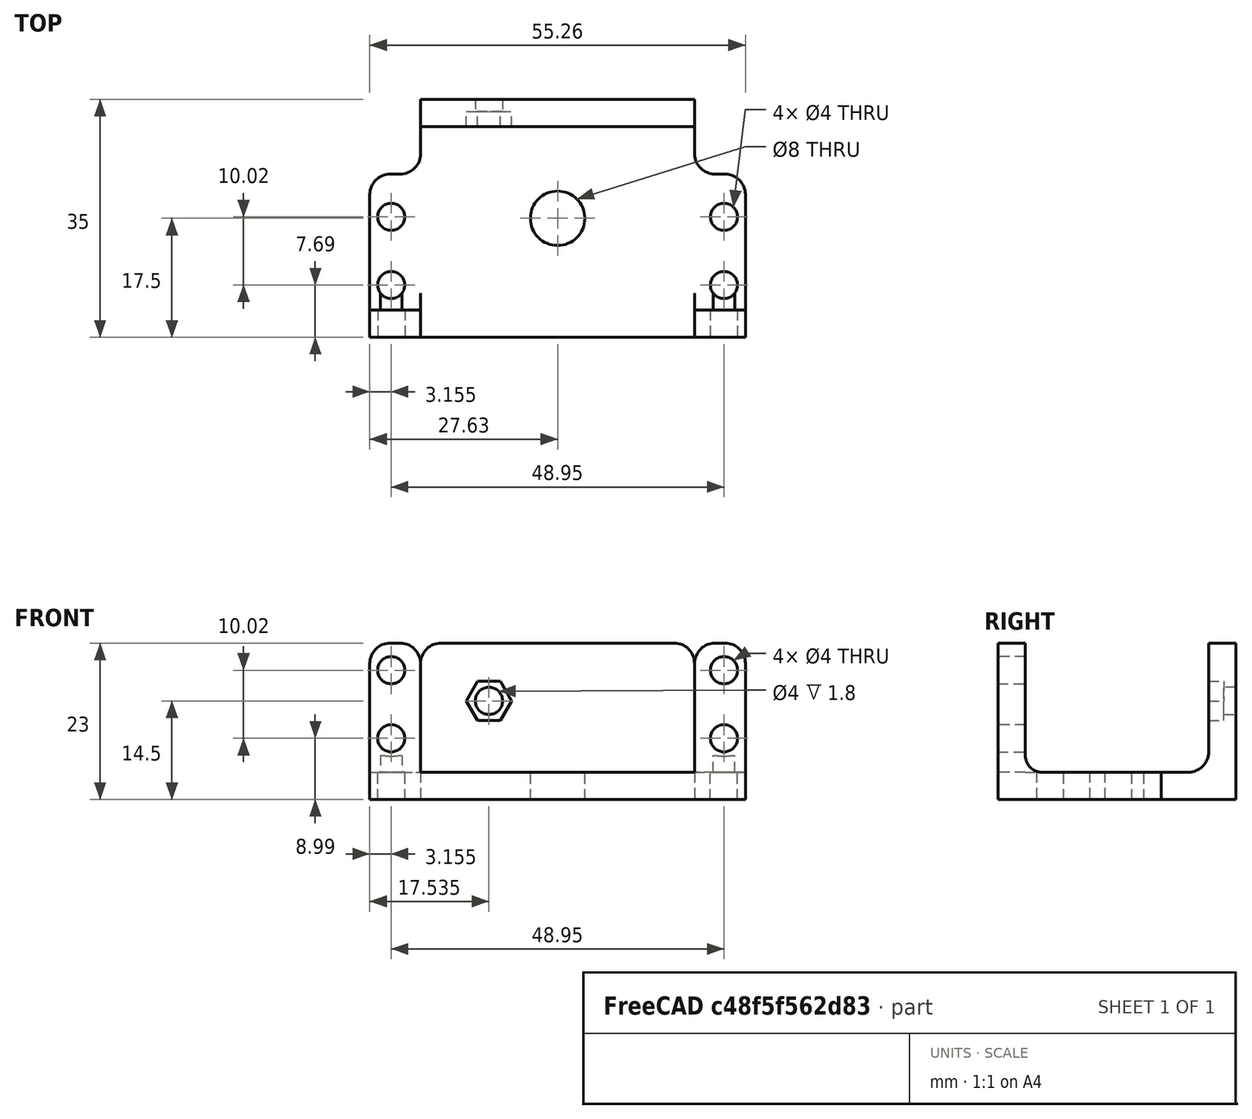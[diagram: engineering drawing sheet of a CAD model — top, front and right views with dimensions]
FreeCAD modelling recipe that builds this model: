
FCSTD DOCUMENT  (FreeCAD 0.17R13519 (Git))
Label: pieza1v4
License: CreativeCommons Attribution-ShareAlike
LicenseURL: http://creativecommons.org/licenses/by-sa/4.0/
objects: Sketcher::SketchObject×8, PartDesign::Pocket×7, PartDesign::Plane×6, PartDesign::Mirrored×3, PartDesign::Fillet×3, PartDesign::Pad×1, Mesh::Feature×1, PartDesign::Body×1, Part::Feature×1
note: 38 computed .brp shape members not serialized (recipe doc carries the construction recipe); baked Part::Feature solids carry a one-line shape summary decoded from their .brp

FEATURE [Sketcher::SketchObject] Sketch
  MapMode = 5
  Placement = pos=(0,0,0) rot=(0.57735,0.57735,0.57735;2.0944rad)
  Support = -> [YZ_Plane]
  sketch-geometry (8):
    g0: LineSegment StartX=-17.5 StartY=23 StartZ=0 EndX=-17.5 EndY=0 EndZ=0
    g1: LineSegment StartX=-17.5 StartY=0 StartZ=0 EndX=17.5 EndY=0 EndZ=0
    g2: LineSegment StartX=17.5 StartY=0 StartZ=0 EndX=17.5 EndY=23 EndZ=0
    g3: LineSegment StartX=17.5 StartY=23 StartZ=0 EndX=13.5 EndY=23 EndZ=0
    g4: LineSegment StartX=13.5 StartY=23 StartZ=0 EndX=13.5 EndY=4 EndZ=0
    g5: LineSegment StartX=13.5 StartY=4 StartZ=0 EndX=-13.5 EndY=4 EndZ=0
    g6: LineSegment StartX=-13.5 StartY=4 StartZ=0 EndX=-13.5 EndY=23 EndZ=0
    g7: LineSegment StartX=-13.5 StartY=23 StartZ=0 EndX=-17.5 EndY=23 EndZ=0
  constraints (24):
    c: PointOnObject(g0,g-1)
    c: Vertical(g0)
    c: Coincident(g0,g1)
    c: PointOnObject(g1,g-1)
    c: Coincident(g1,g2)
    c: Vertical(g2)
    c: Coincident(g2,g3)
    c: Horizontal(g3)
    c: Coincident(g3,g4)
    c: Vertical(g4)
    c: Coincident(g4,g5)
    c: Horizontal(g5)
    c: Coincident(g5,g6)
    c: Vertical(g6)
    c: Coincident(g6,g7)
    c: Coincident(g7,g0)
    c: Horizontal(g7)
    c: Symmetric(g0,g1,g-2)
    c: Equal(g7,g3)
    c: DistanceX(g7,g7) = 4
    c: DistanceY(g0,g5) = 4
    c: DistanceX(g1,g1) = 35
    c: Equal(g0,g2)
    c: DistanceY(g0,g0) = 23
FEATURE [PartDesign::Pad] Pad
  Length = 55.25
  Length2 = 100
  Midplane = true
  Placement = pos=(0,0,0) rot=(0.57735,0.57735,0.57735;2.0944rad)
  Profile = -> Sketch
  Type = 0
FEATURE [PartDesign::Plane] DatumPlane
  MapMode = 5
  Placement = pos=(0,0,23) rot=(0,0,-1;1.5708rad)
  Support = -> [Pad]
FEATURE [Sketcher::SketchObject] Sketch001
  ExternalGeometry = -> [Pad]
  MapMode = 5
  Placement = pos=(0,0,23) rot=(0,0,-1;1.5708rad)
  Support = -> [DatumPlane]
  sketch-geometry (4):
    g0: LineSegment StartX=13.5 StartY=-20.15 StartZ=0 EndX=17.5 EndY=-20.15 EndZ=0
    g1: LineSegment StartX=17.5 StartY=-20.15 StartZ=0 EndX=17.5 EndY=20.15 EndZ=0
    g2: LineSegment StartX=17.5 StartY=20.15 StartZ=0 EndX=13.5 EndY=20.15 EndZ=0
    g3: LineSegment StartX=13.5 StartY=20.15 StartZ=0 EndX=13.5 EndY=-20.15 EndZ=0
  constraints (12):
    c: Coincident(g0,g1)
    c: Coincident(g1,g2)
    c: Coincident(g2,g3)
    c: Coincident(g3,g0)
    c: Horizontal(g0)
    c: Horizontal(g2)
    c: Vertical(g1)
    c: Vertical(g3)
    c: Symmetric(g0,g2,g-1)
    c: DistanceY(g3,g3) = 40.3
    c: DistanceX(g2,g2) = 4
    c: PointOnObject(g1,g-3)
FEATURE [PartDesign::Pocket] Pocket
  BaseFeature = -> Pad
  Length = 0
  Length2 = 100
  Placement = pos=(0,0,0) rot=(0.57735,0.57735,0.57735;2.0944rad)
  Profile = -> Sketch001
  Type = 3
  UpToFace = -> Pad [Face6]
FEATURE [Sketcher::SketchObject] Sketch002
  ExternalGeometry = -> [Pocket]
  MapMode = 5
  Placement = pos=(0,0,23) rot=(0,0,-1;1.5708rad)
  Support = -> [DatumPlane]
  sketch-geometry (4):
    g0: LineSegment StartX=-17.5 StartY=27.625 StartZ=0 EndX=-6.5 EndY=27.625 EndZ=0
    g1: LineSegment StartX=-6.5 StartY=27.625 StartZ=0 EndX=-6.5 EndY=20.145 EndZ=0
    g2: LineSegment StartX=-6.5 StartY=20.145 StartZ=0 EndX=-17.5 EndY=20.145 EndZ=0
    g3: LineSegment StartX=-17.5 StartY=20.145 StartZ=0 EndX=-17.5 EndY=27.625 EndZ=0
  constraints (11):
    c: Coincident(g0,g1)
    c: Coincident(g1,g2)
    c: Coincident(g2,g3)
    c: Coincident(g3,g0)
    c: Horizontal(g0)
    c: Horizontal(g2)
    c: Vertical(g1)
    c: Vertical(g3)
    c: Coincident(g0,g-3)
    c: DistanceX(g0,g0) = 11
    c: DistanceY(g3,g3) = 7.48
FEATURE [PartDesign::Pocket] Pocket001
  BaseFeature = -> Pocket
  Length = 5
  Length2 = 100
  Placement = pos=(0,0,0) rot=(0.57735,0.57735,0.57735;2.0944rad)
  Profile = -> Sketch002
  Type = 1
FEATURE [PartDesign::Mirrored] Mirrored
  BaseFeature = -> Pocket001
  MirrorPlane = -> YZ_Plane
  Originals = -> [Pocket001]
  Placement = pos=(0,0,0) rot=(0.57735,0.57735,0.57735;2.0944rad)
FEATURE [PartDesign::Plane] DatumPlane001
  MapMode = 5
  Placement = pos=(0,-17.5,0) rot=(-0.57735,-0.57735,0.57735;4.18879rad)
  Support = -> [Mirrored]
FEATURE [Mesh::Feature] Futaba3003
  Placement = pos=(0,8.1,14.1) rot=(0,0.707107,-0.707107;3.14159rad)
FEATURE [Sketcher::SketchObject] Sketch003
  ExternalGeometry = -> [Mirrored]
  MapMode = 5
  Placement = pos=(0,-17.5,0) rot=(0.57735,0.57735,-0.57735;2.0944rad)
  Support = -> [DatumPlane001]
  sketch-geometry (3):
    g0: LineSegment [constr] StartX=-24.8913 StartY=-24.475 StartZ=0 EndX=1.6681 EndY=-24.475 EndZ=0
    g1: Circle CenterX=-19.01 CenterY=-24.475 CenterZ=0 NormalX=0 NormalY=0 NormalZ=1 AngleXU=0 Radius=2
    g2: Circle CenterX=-8.99 CenterY=-24.475 CenterZ=0 NormalX=0 NormalY=0 NormalZ=1 AngleXU=0 Radius=2
  constraints (8):
    c: Horizontal(g0)
    c: DistanceY(g-3,g0) = 3.15
    c: PointOnObject(g1,g0)
    c: PointOnObject(g2,g0)
    c: DistanceX(g-3,g1) = 3.99
    c: Equal(g1,g2)
    c: Radius(g1) = 2
    c: DistanceX(g1,g2) = 10.02
FEATURE [PartDesign::Pocket] Pocket002
  BaseFeature = -> Mirrored
  Length = 5
  Length2 = 100
  Placement = pos=(0,0,0) rot=(0.57735,0.57735,0.57735;2.0944rad)
  Profile = -> Sketch003
  Type = 0
FEATURE [PartDesign::Mirrored] Mirrored001
  BaseFeature = -> Pocket002
  MirrorPlane = -> YZ_Plane
  Originals = -> [Pocket002]
  Placement = pos=(0,0,0) rot=(0.57735,0.57735,0.57735;2.0944rad)
FEATURE [PartDesign::Plane] DatumPlane002
  MapMode = 5
  Placement = pos=(0,0,4) rot=(0,0,-1;1.5708rad)
  Support = -> [Mirrored001]
FEATURE [Sketcher::SketchObject] Sketch004
  ExternalGeometry = -> [Mirrored001]
  MapMode = 5
  Placement = pos=(0,0,4) rot=(0,0,-1;1.5708rad)
  Support = -> [DatumPlane002]
  sketch-geometry (3):
    g0: LineSegment [constr] StartX=13.5 StartY=-24.475 StartZ=0 EndX=-8.14904 EndY=-24.475 EndZ=0
    g1: Circle CenterX=9.81 CenterY=-24.475 CenterZ=0 NormalX=0 NormalY=0 NormalZ=1 AngleXU=0 Radius=2
    g2: Circle CenterX=-0.21 CenterY=-24.475 CenterZ=0 NormalX=0 NormalY=0 NormalZ=1 AngleXU=0 Radius=2
  constraints (9):
    c: PointOnObject(g0,g-3)
    c: Horizontal(g0)
    c: PointOnObject(g1,g0)
    c: PointOnObject(g2,g0)
    c: DistanceY(g-4,g0) = 3.15
    c: DistanceX(g1,g-4) = 3.69
    c: Equal(g1,g2)
    c: Radius(g1) = 2
    c: DistanceX(g2,g1) = 10.02
FEATURE [PartDesign::Pocket] Pocket003
  BaseFeature = -> Mirrored001
  Length = 5
  Length2 = 100
  Placement = pos=(0,0,0) rot=(0.57735,0.57735,0.57735;2.0944rad)
  Profile = -> Sketch004
  Type = 0
FEATURE [PartDesign::Mirrored] Mirrored002
  BaseFeature = -> Pocket003
  MirrorPlane = -> YZ_Plane
  Originals = -> [Pocket003]
  Placement = pos=(0,0,0) rot=(0.57735,0.57735,0.57735;2.0944rad)
FEATURE [PartDesign::Plane] DatumPlane003
  MapMode = 5
  Placement = pos=(0,13.5,0) rot=(-0.57735,-0.57735,0.57735;4.18879rad)
  Support = -> [Mirrored002]
FEATURE [Sketcher::SketchObject] Sketch005
  ExternalGeometry = -> [Mirrored002]
  MapMode = 5
  Placement = pos=(0,13.5,0) rot=(0.57735,0.57735,-0.57735;2.0944rad)
  Support = -> [DatumPlane003]
  sketch-geometry (7):
    g0: LineSegment StartX=-14.5 StartY=-6.745 StartZ=0 EndX=-17.4012 EndY=-8.42 EndZ=0
    g1: LineSegment StartX=-17.4012 StartY=-8.42 StartZ=0 EndX=-17.4012 EndY=-11.77 EndZ=0
    g2: LineSegment StartX=-17.4012 StartY=-11.77 StartZ=0 EndX=-14.5 EndY=-13.445 EndZ=0
    g3: LineSegment StartX=-14.5 StartY=-13.445 StartZ=0 EndX=-11.5988 EndY=-11.77 EndZ=0
    g4: LineSegment StartX=-11.5988 StartY=-11.77 StartZ=0 EndX=-11.5988 EndY=-8.42 EndZ=0
    g5: LineSegment StartX=-11.5988 StartY=-8.42 StartZ=0 EndX=-14.5 EndY=-6.745 EndZ=0
    g6: Circle [constr] CenterX=-14.5 CenterY=-10.095 CenterZ=0 NormalX=0 NormalY=0 NormalZ=1 AngleXU=0 Radius=3.35
  constraints (17):
    c: Coincident(g0,g1)
    c: Coincident(g1,g2)
    c: Coincident(g2,g3)
    c: Coincident(g3,g4)
    c: Coincident(g4,g5)
    c: Coincident(g5,g0)
    c: Equal(g0, g1-g5) x5
    c: PointOnObject(g0,g6)
    c: PointOnObject(g1,g6)
    c: PointOnObject(g2,g6)
    c: PointOnObject(g3,g6)
    c: PointOnObject(g4,g6)
    c: PointOnObject(g5,g6)
    c: Vertical(g1)
    c: DistanceX(g-4,g6) = 8.5
    c: DistanceY(g-4,g6) = 10.05
    c: DistanceY(g2,g0) = 6.7
FEATURE [PartDesign::Pocket] Pocket004
  BaseFeature = -> Mirrored002
  Length = 2.2
  Length2 = 100
  Placement = pos=(0,0,0) rot=(0.57735,0.57735,0.57735;2.0944rad)
  Profile = -> Sketch005
  Type = 0
FEATURE [PartDesign::Plane] DatumPlane004
  MapMode = 5
  Placement = pos=(0,15.7,0) rot=(-0.57735,-0.57735,0.57735;4.18879rad)
  Support = -> [Pocket004]
FEATURE [Sketcher::SketchObject] Sketch006
  ExternalGeometry = -> [Pocket004]
  MapMode = 5
  Placement = pos=(0,15.7,0) rot=(-0.57735,-0.57735,0.57735;4.18879rad)
  Support = -> [DatumPlane004]
  sketch-geometry (3):
    g0: Circle CenterX=-14.5 CenterY=-10.095 CenterZ=0 NormalX=0 NormalY=0 NormalZ=1 AngleXU=0 Radius=2
    g1: LineSegment [constr] StartX=-14.5 StartY=-6.745 StartZ=0 EndX=-14.5 EndY=-13.445 EndZ=0
    g2: LineSegment [constr] StartX=-17.4012 StartY=-8.42 StartZ=0 EndX=-11.5988 EndY=-11.77 EndZ=0
  constraints (7):
    c: Coincident(g1,g-4)
    c: Coincident(g1,g-7)
    c: Coincident(g2,g-8)
    c: Coincident(g2,g-6)
    c: PointOnObject(g0,g1)
    c: PointOnObject(g0,g2)
    c: Radius(g0) = 2
FEATURE [PartDesign::Pocket] Pocket005
  BaseFeature = -> Pocket004
  Length = 0
  Length2 = 100
  Placement = pos=(0,0,0) rot=(0.57735,0.57735,0.57735;2.0944rad)
  Profile = -> Sketch006
  Type = 2
FEATURE [PartDesign::Fillet] Fillet
  Base = -> Pocket005 [Edge18,Edge13,Edge38,Edge32,Edge35,Edge64,Edge69,Edge62,Edge60,Edge16]
  BaseFeature = -> Pocket005
  Placement = pos=(0,0,0) rot=(0.57735,0.57735,0.57735;2.0944rad)
  Radius = 3
FEATURE [PartDesign::Fillet] Fillet001
  Base = -> Fillet [Edge69,Edge65]
  BaseFeature = -> Fillet
  Placement = pos=(0,0,0) rot=(0.57735,0.57735,0.57735;2.0944rad)
  Radius = 2.5
FEATURE [PartDesign::Fillet] Fillet002
  Base = -> Fillet001 [Edge28]
  BaseFeature = -> Fillet001
  Placement = pos=(0,0,0) rot=(0.57735,0.57735,0.57735;2.0944rad)
  Radius = 3
FEATURE [PartDesign::Plane] DatumPlane005
  MapMode = 5
  Placement = pos=(0,0,4) rot=(0,0,-1;1.5708rad)
  Support = -> [Fillet002]
FEATURE [Sketcher::SketchObject] Sketch007
  MapMode = 5
  Placement = pos=(0,0,4) rot=(0,0,-1;1.5708rad)
  Support = -> [DatumPlane005]
  sketch-geometry (1):
    g0: Circle CenterX=0 CenterY=0 CenterZ=0 NormalX=0 NormalY=0 NormalZ=1 AngleXU=0 Radius=4
  constraints (2):
    c: Coincident(g0,g-1)
    c: Radius(g0) = 4
FEATURE [PartDesign::Pocket] Pocket005002
  BaseFeature = -> Fillet002
  Length = 5
  Length2 = 100
  Placement = pos=(0,0,0) rot=(0.57735,0.57735,0.57735;2.0944rad)
  Profile = -> Sketch007
  Type = 2
FEATURE [PartDesign::Body] Body
  Group = -> [Sketch,Pad,DatumPlane,Sketch001,Pocket,Sketch002,Pocket001,Mirrored,DatumPlane001,Sketch003,Pocket002,Mirrored001,DatumPlane002,Sketch004,Pocket003,Mirrored002,DatumPlane003,Sketch005,Pocket004,DatumPlane004,Sketch006,Pocket005,Fillet,Fillet001,Fillet002,DatumPlane005,Sketch007,Pocket005002]
  Origin = -> Origin
  Tip = -> Pocket005002
FEATURE [Part::Feature] Body001
  shape: bbox 55.25 x 35 x 23 mm, 55 faces (baked)
